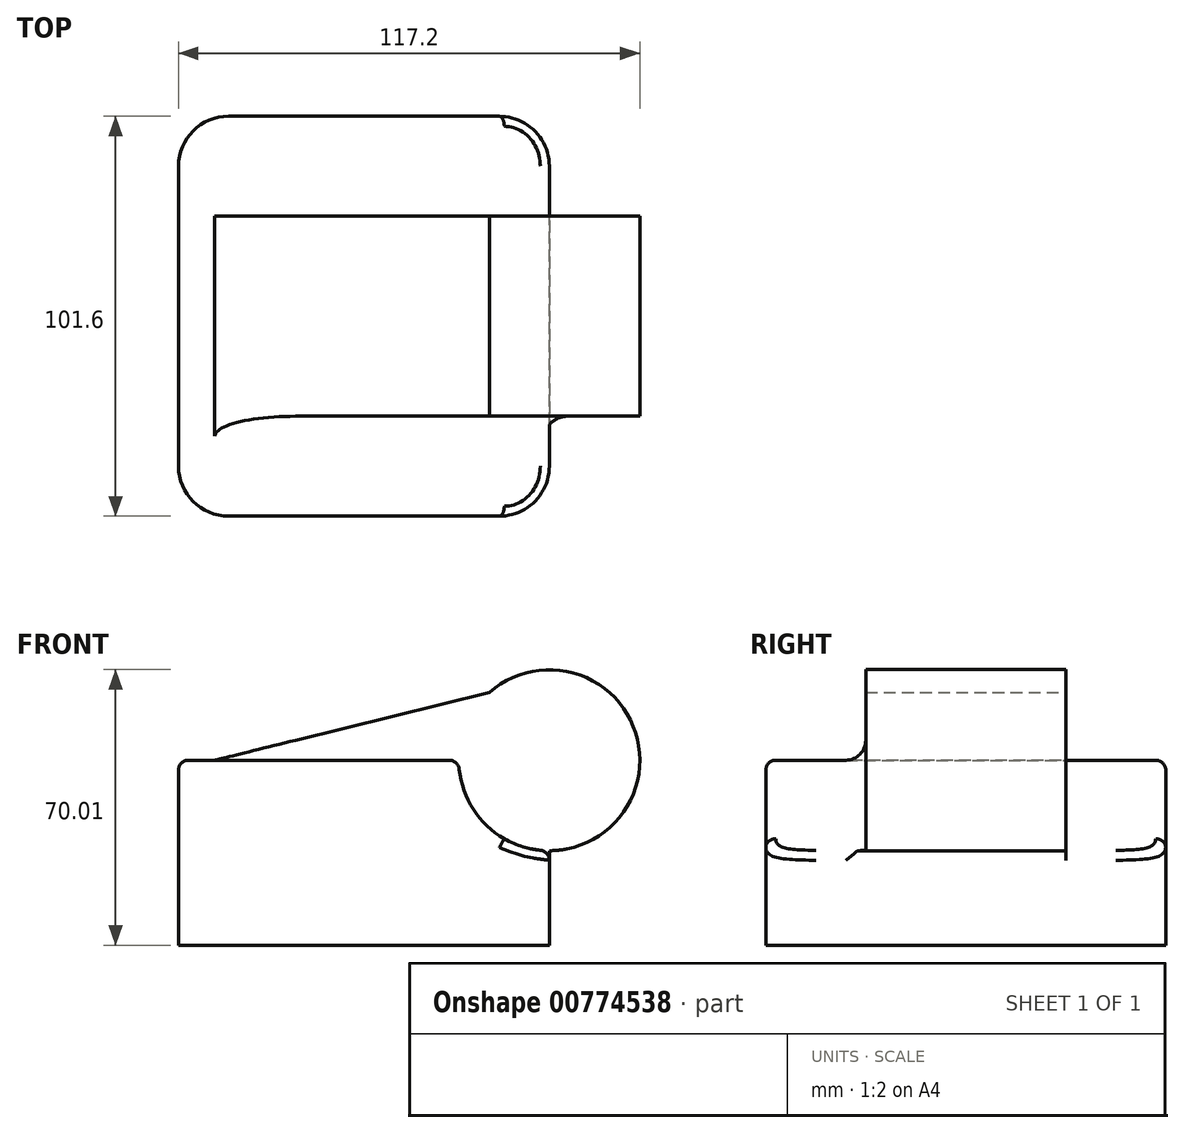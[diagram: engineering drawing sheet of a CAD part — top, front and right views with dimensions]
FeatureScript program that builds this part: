
annotation { "Feature Type Name" : "Feature", "Feature Type Description" : "" }
export const myFeature = defineFeature(function(context is Context, id is Id, definition is map)
    precondition{}
    {
        {
            var Q0;
            Q0=qCreatedBy(makeId("Front.planeOp"),FACE);
            var sketch = newSketch(context, id + "F0", { "sketchPlane" : qUnion([Q0])});
            skLineSegment(sketch, "E0.bottom", {"start": v(47.1, 23.5) * mm, "end": v(-47.1, 23.5) * mm});
            skLineSegment(sketch, "E0.top", {"start": v(47.1, -23.5) * mm, "end": v(-47.1, -23.5) * mm});
            skLineSegment(sketch, "E0.left", {"start": v(47.1, 23.5) * mm, "end": v(47.1, -23.5) * mm});
            skLineSegment(sketch, "E0.right", {"start": v(-47.1, 23.5) * mm, "end": v(-47.1, -23.5) * mm});
            skPoint(sketch, "E0.middle", {"position": v(0, 0) * mm});
            skCircle(sketch, "E1", {"center": v(47.1, 23.5) * mm, "radius": 23 * mm});
            skLineSegment(sketch, "E2", {"start": v(-37.88, 23.5) * mm, "end": v(31.9, 40.76) * mm});
            skSolve(sketch);
        }
        {
            var Q0;
            {var subQ1=sQuery(id+"F0.wireOp",EDGE,"E0.top");Q0=makeQuery(id+"F0.imprint","IMPRINT",FACE,{"disambiguationData":[TD([[makeQuery(id+"F0.imprint","IMPRINT",EDGE,{"derivedFrom":subQ1}),-1.0]])]});}
            extrude(context, id + "F1", {"entities" : qUnion([Q0]), "endBound" : BoundingType.SYMMETRIC, "oppositeDirection" : true, "depth" : 101.6 * mm, "offsetDistance" : 25.4 * mm});
        }
        {
            var Q0;
            Q0 = qSketchRegion(id + "F0", true);
            extrude(context, id + "F2", {"entities" : qUnion([Q0]), "operationType" : NewBodyOperationType.ADD, "endBound" : BoundingType.SYMMETRIC, "depth" : 50.8 * mm, "offsetDistance" : 25.4 * mm});
        }
        {
            var Q0;
            Q0=makeQuery(id+"F1.opExtrude","CAP_EDGE",EDGE,{"disambiguationData":[OSD([sQuery(id+"F0.wireOp",EDGE,"E0.left")])],"isStart":true});
            var Q1;
            Q1=makeQuery(id+"F1.opExtrude","CAP_EDGE",EDGE,{"disambiguationData":[OSD([sQuery(id+"F0.wireOp",EDGE,"E0.right")])],"isStart":true});
            var Q2;
            Q2=makeQuery(id+"F1.opExtrude","CAP_EDGE",EDGE,{"disambiguationData":[OSD([sQuery(id+"F0.wireOp",EDGE,"E0.right")])],"isStart":false});
            var Q3;
            Q3=makeQuery(id+"F1.opExtrude","CAP_EDGE",EDGE,{"disambiguationData":[OSD([sQuery(id+"F0.wireOp",EDGE,"E0.left")])],"isStart":false});
            fillet(context, id + "F3", {"entities" : qUnion([Q0, Q1, Q2, Q3]), "radius" : 12.7 * mm, "tangentPropagation" : true, "allowEdgeOverflow" : false});
        }
        {
            var Q0;
            {var subQ0=sQuery(id+"F0.wireOp",EDGE,"E1");var subQ1=sQuery(id+"F0.wireOp",EDGE,"E0.right");var subQ2=sQuery(id+"F0.wireOp",EDGE,"E0.left");var subQ3=sQuery(id+"F0.wireOp",EDGE,"E0.top");var subQ4=sQuery(id+"F0.wireOp",EDGE,"E0.bottom");Q0=makeQuery(id+"F2.boolean.opBoolean","SPLIT",EDGE,{"disambiguationData":[TD([makeQuery(id+"F1.opExtrude","CAP_FACE",FACE,{"disambiguationData":[OSD([subQ4,subQ3,subQ2,subQ1,subQ0])],"isStart":true})])],"derivedFrom":makeQuery(id+"F1.opExtrude","SWEPT_EDGE",EDGE,{"disambiguationData":[OSD([subQ2,subQ0])]})});}
            var Q1;
            {var subQ0=sQuery(id+"F0.wireOp",EDGE,"E1");var subQ1=sQuery(id+"F0.wireOp",EDGE,"E0.right");var subQ2=sQuery(id+"F0.wireOp",EDGE,"E0.left");var subQ3=sQuery(id+"F0.wireOp",EDGE,"E0.top");var subQ4=sQuery(id+"F0.wireOp",EDGE,"E0.bottom");Q1=makeQuery(id+"F3.opFillet","BLEND_EDGE",EDGE,{"blendedFrom":[makeQuery(id+"F1.opExtrude","CAP_EDGE",EDGE,{"disambiguationData":[OSD([subQ2])],"isStart":true}),makeQuery(id+"F2.boolean.opBoolean","SPLIT",FACE,{"disambiguationData":[TD([makeQuery(id+"F1.opExtrude","CAP_FACE",FACE,{"disambiguationData":[OSD([subQ4,subQ3,subQ2,subQ1,subQ0])],"isStart":true})])],"derivedFrom":makeQuery(id+"F1.opExtrude","SWEPT_FACE",FACE,{"disambiguationData":[OSD([subQ0])]})})],"blendedInto":[makeQuery(id+"F2.boolean.opBoolean","SPLIT",FACE,{"disambiguationData":[TD([makeQuery(id+"F1.opExtrude","CAP_FACE",FACE,{"disambiguationData":[OSD([subQ4,subQ3,subQ2,subQ1,subQ0])],"isStart":true})])],"derivedFrom":makeQuery(id+"F1.opExtrude","SWEPT_FACE",FACE,{"disambiguationData":[OSD([subQ0])]})})]});}
            var Q2;
            Q2=makeQuery(id+"F1.opExtrude","CAP_EDGE",EDGE,{"disambiguationData":[OSD([sQuery(id+"F0.wireOp",EDGE,"E0.bottom")])],"isStart":true});
            var Q3;
            Q3=makeQuery(id+"F3.opFillet","BLEND_EDGE",EDGE,{"blendedFrom":[makeQuery(id+"F1.opExtrude","CAP_EDGE",EDGE,{"disambiguationData":[OSD([sQuery(id+"F0.wireOp",EDGE,"E0.right")])],"isStart":true}),makeQuery(id+"F1.opExtrude","SWEPT_FACE",FACE,{"disambiguationData":[OSD([sQuery(id+"F0.wireOp",EDGE,"E0.bottom")])]})],"blendedInto":[makeQuery(id+"F1.opExtrude","SWEPT_FACE",FACE,{"disambiguationData":[OSD([sQuery(id+"F0.wireOp",EDGE,"E0.bottom")])]})]});
            var Q4;
            {var subQ0=sQuery(id+"F0.wireOp",EDGE,"E0.bottom");var subQ1=sQuery(id+"F0.wireOp",EDGE,"E1");var subQ2=sQuery(id+"F0.wireOp",EDGE,"E0.right");var subQ3=sQuery(id+"F0.wireOp",EDGE,"E0.left");var subQ4=sQuery(id+"F0.wireOp",EDGE,"E0.top");Q4=makeQuery(id+"F2.boolean.opBoolean","SPLIT",EDGE,{"disambiguationData":[TD([makeQuery(id+"F1.opExtrude","CAP_FACE",FACE,{"disambiguationData":[OSD([subQ0,subQ4,subQ3,subQ2,subQ1])],"isStart":false})])],"derivedFrom":makeQuery(id+"F1.opExtrude","SWEPT_EDGE",EDGE,{"disambiguationData":[OSD([subQ0,subQ1])]})});}
            var Q5;
            Q5=makeQuery(id+"F1.opExtrude","CAP_EDGE",EDGE,{"disambiguationData":[OSD([sQuery(id+"F0.wireOp",EDGE,"E1")])],"isStart":false});
            var Q6;
            {var subQ0=sQuery(id+"F0.wireOp",EDGE,"E0.left");var subQ1=sQuery(id+"F0.wireOp",EDGE,"E1");var subQ2=sQuery(id+"F0.wireOp",EDGE,"E0.right");var subQ3=sQuery(id+"F0.wireOp",EDGE,"E0.top");var subQ4=sQuery(id+"F0.wireOp",EDGE,"E0.bottom");Q6=makeQuery(id+"F3.opFillet","BLEND_EDGE",EDGE,{"blendedFrom":[makeQuery(id+"F1.opExtrude","CAP_EDGE",EDGE,{"disambiguationData":[OSD([subQ0])],"isStart":false}),makeQuery(id+"F2.boolean.opBoolean","SPLIT",FACE,{"disambiguationData":[TD([makeQuery(id+"F1.opExtrude","CAP_FACE",FACE,{"disambiguationData":[OSD([subQ4,subQ3,subQ0,subQ2,subQ1])],"isStart":false})])],"derivedFrom":makeQuery(id+"F1.opExtrude","SWEPT_FACE",FACE,{"disambiguationData":[OSD([subQ1])]})})],"blendedInto":[makeQuery(id+"F2.boolean.opBoolean","SPLIT",FACE,{"disambiguationData":[TD([makeQuery(id+"F1.opExtrude","CAP_FACE",FACE,{"disambiguationData":[OSD([subQ4,subQ3,subQ0,subQ2,subQ1])],"isStart":false})])],"derivedFrom":makeQuery(id+"F1.opExtrude","SWEPT_FACE",FACE,{"disambiguationData":[OSD([subQ1])]})})]});}
            var Q7;
            {var subQ0=sQuery(id+"F0.wireOp",EDGE,"E0.bottom");var subQ1=sQuery(id+"F0.wireOp",EDGE,"E1");var subQ2=sQuery(id+"F0.wireOp",EDGE,"E0.right");var subQ3=sQuery(id+"F0.wireOp",EDGE,"E0.left");var subQ4=sQuery(id+"F0.wireOp",EDGE,"E0.top");Q7=makeQuery(id+"F2.boolean.opBoolean","SPLIT",EDGE,{"disambiguationData":[TD([makeQuery(id+"F1.opExtrude","CAP_FACE",FACE,{"disambiguationData":[OSD([subQ0,subQ4,subQ3,subQ2,subQ1])],"isStart":true})])],"derivedFrom":makeQuery(id+"F1.opExtrude","SWEPT_EDGE",EDGE,{"disambiguationData":[OSD([subQ0,subQ1])]})});}
            fillet(context, id + "F4", {"entities" : qUnion([Q0, Q1, Q2, Q3, Q4, Q5, Q6, Q7]), "radius" : 2.54 * mm, "tangentPropagation" : true, "allowEdgeOverflow" : false});
        }
        {
            var Q0;
            {var subQ0=sQuery(id+"F0.wireOp",EDGE,"E1");Q0=makeQuery(id+"F2.boolean.opBoolean","INTERSECT",EDGE,{"derivedFrom":[makeQuery(id+"F1.opExtrude","SWEPT_FACE",FACE,{"disambiguationData":[OSD([subQ0])]}),makeQuery(id+"F2.opExtrude","CAP_FACE",FACE,{"disambiguationData":[OSD([sQuery(id+"F0.wireOp",EDGE,"E0.bottom"),sQuery(id+"F0.wireOp",EDGE,"E0.top"),sQuery(id+"F0.wireOp",EDGE,"E0.left"),sQuery(id+"F0.wireOp",EDGE,"E0.right"),subQ0,sQuery(id+"F0.wireOp",EDGE,"E2")])],"isStart":false})]});}
            var Q1;
            {var subQ0=sQuery(id+"F0.wireOp",EDGE,"E1");var subQ1=sQuery(id+"F0.wireOp",EDGE,"E0.right");var subQ2=sQuery(id+"F0.wireOp",EDGE,"E0.left");var subQ3=sQuery(id+"F0.wireOp",EDGE,"E0.top");var subQ4=sQuery(id+"F0.wireOp",EDGE,"E0.bottom");var subQ5=makeQuery(id+"F2.opExtrude","CAP_FACE",FACE,{"disambiguationData":[OSD([subQ4,subQ3,subQ2,subQ1,subQ0,sQuery(id+"F0.wireOp",EDGE,"E2")])],"isStart":false});Q1=makeQuery(id+"F4.opFillet","BLEND_EDGE",EDGE,{"blendedFrom":[makeQuery(id+"F2.boolean.opBoolean","SPLIT",EDGE,{"disambiguationData":[TD([makeQuery(id+"F1.opExtrude","CAP_FACE",FACE,{"disambiguationData":[OSD([subQ4,subQ3,subQ2,subQ1,subQ0])],"isStart":true})])],"derivedFrom":makeQuery(id+"F1.opExtrude","SWEPT_EDGE",EDGE,{"disambiguationData":[OSD([subQ4,subQ0])]})}),subQ5],"blendedInto":[subQ5]});}
            var Q2;
            {var subQ0=sQuery(id+"F0.wireOp",EDGE,"E0.bottom");Q2=makeQuery(id+"F2.boolean.opBoolean","INTERSECT",EDGE,{"derivedFrom":[makeQuery(id+"F1.opExtrude","SWEPT_FACE",FACE,{"disambiguationData":[OSD([subQ0])]}),makeQuery(id+"F2.opExtrude","CAP_FACE",FACE,{"disambiguationData":[OSD([subQ0,sQuery(id+"F0.wireOp",EDGE,"E0.top"),sQuery(id+"F0.wireOp",EDGE,"E0.left"),sQuery(id+"F0.wireOp",EDGE,"E0.right"),sQuery(id+"F0.wireOp",EDGE,"E1"),sQuery(id+"F0.wireOp",EDGE,"E2")])],"isStart":false})]});}
            var Q3;
            Q3=makeQuery(id+"F2.opExtrude","SWEPT_EDGE",EDGE,{"disambiguationData":[OSD([sQuery(id+"F0.wireOp",EDGE,"E0.bottom"),sQuery(id+"F0.wireOp",EDGE,"E2")])]});
            fillet(context, id + "F5", {"entities" : qUnion([Q0, Q1, Q2, Q3]), "radius" : 5.08 * mm, "tangentPropagation" : true, "allowEdgeOverflow" : false});
        }
    });
